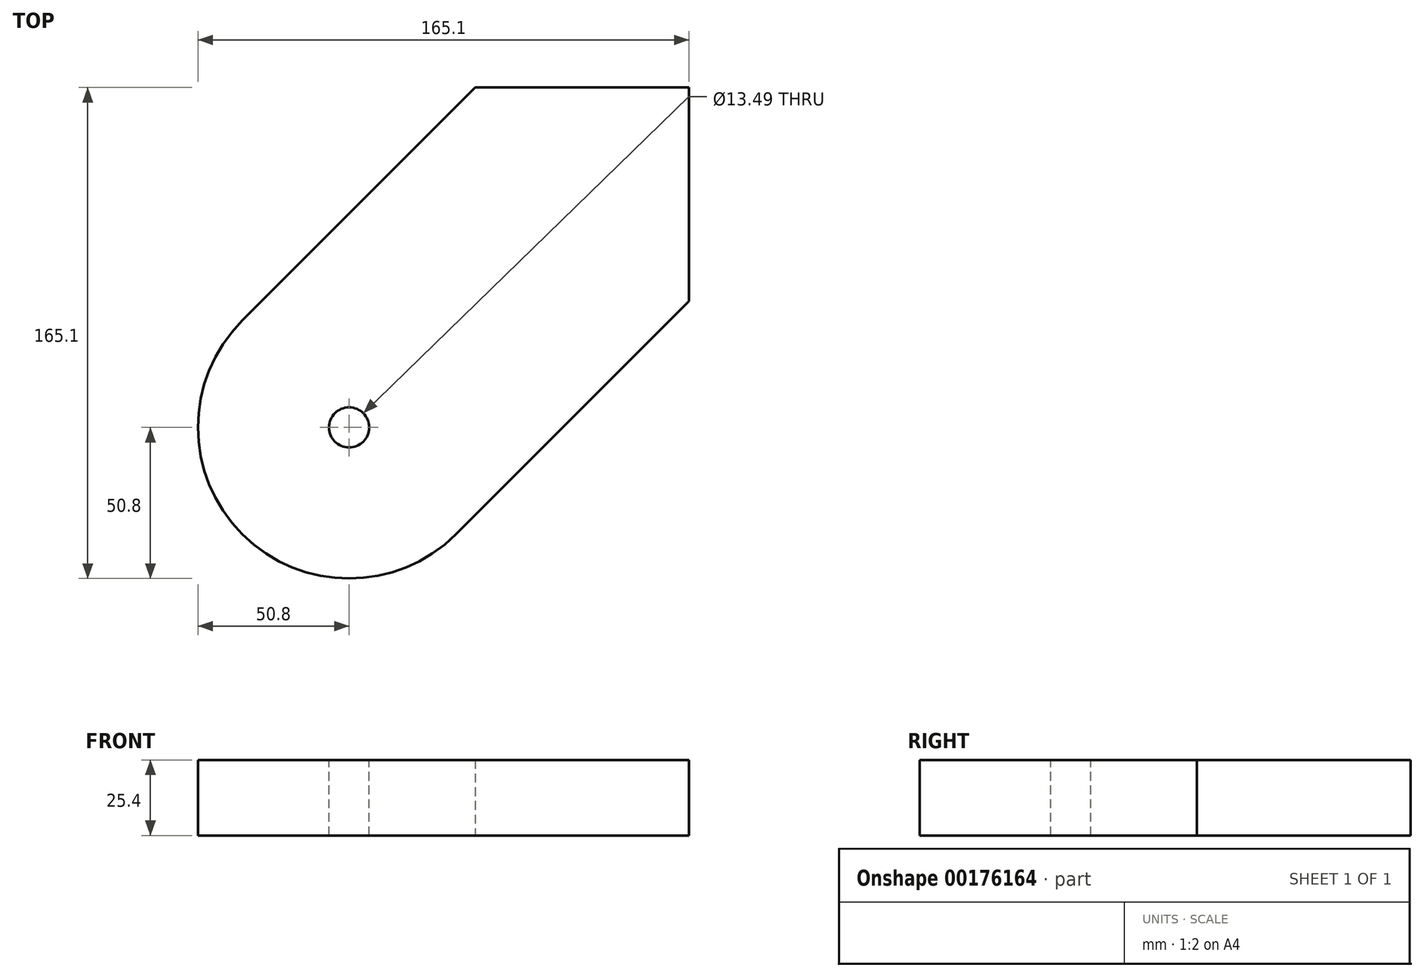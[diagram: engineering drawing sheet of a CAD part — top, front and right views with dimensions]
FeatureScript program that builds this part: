
annotation { "Feature Type Name" : "Feature", "Feature Type Description" : "" }
export const myFeature = defineFeature(function(context is Context, id is Id, definition is map)
    precondition{}
    {
        {
            var Q0;
            Q0=qCreatedBy(makeId("Top.planeOp"),FACE);
            var sketch = newSketch(context, id + "F0", { "sketchPlane" : qUnion([Q0])});
            skArc(sketch, "E0", {"start": v(-35.92, 35.92) * mm, "mid": v(-35.92, -35.92) * mm, "end": v(35.92, -35.92) * mm});
            skLineSegment(sketch, "E1", {"start": v(-35.92, 35.92) * mm, "end": v(42.46, 114.3) * mm});
            skLineSegment(sketch, "E2", {"start": v(42.46, 114.3) * mm, "end": v(114.3, 114.3) * mm});
            skLineSegment(sketch, "E3", {"start": v(114.3, 114.3) * mm, "end": v(114.3, 42.46) * mm});
            skLineSegment(sketch, "E4", {"start": v(114.3, 42.46) * mm, "end": v(35.92, -35.92) * mm});
            skSolve(sketch);
        }
        {
            var Q0;
            Q0 = qSketchRegion(id + "F0", true);
            extrude(context, id + "F1", {"entities" : qUnion([Q0]), "depth" : 25.4 * mm});
        }
        {
            var Q0;
            Q0=makeQuery(id+"F1.opExtrude","CAP_FACE",FACE,{"disambiguationData":[OSD([sQuery(id+"F0.wireOp",EDGE,"E0"),sQuery(id+"F0.wireOp",EDGE,"E1"),sQuery(id+"F0.wireOp",EDGE,"E2"),sQuery(id+"F0.wireOp",EDGE,"E3"),sQuery(id+"F0.wireOp",EDGE,"E4")])],"isStart":false});
            var sketch = newSketch(context, id + "F2", { "sketchPlane" : qUnion([Q0])});
            skPoint(sketch, "E5", {"position": v(0, 0) * mm});
            skSolve(sketch);
        }
        {
            var Q0;
            Q0=sQuery(id+"F2.wireOp",VERTEX,"E5");
            var Q1;
            Q1=makeQuery(id+"F1.opExtrude","SWEPT_BODY",BODY,{"disambiguationData":[OSD([sQuery(id+"F0.wireOp",EDGE,"E0"),sQuery(id+"F0.wireOp",EDGE,"E1"),sQuery(id+"F0.wireOp",EDGE,"E2"),sQuery(id+"F0.wireOp",EDGE,"E3"),sQuery(id+"F0.wireOp",EDGE,"E4")])]});
            hole(context, id + "F3", {"style" : HoleStyle.SIMPLE, "endStyle" : HoleEndStyle.THROUGH, "standardTappedOrClearance" : lookupTablePath({ "standard" : "ANSI", "fit" : "Normal (ASME)", "size" : "1/2", "type" : "Clearance" }), "standardBlindInLast" : lookupTablePath({ "fit" : "Free", "standard" : "ANSI", "size" : "1/2", "type" : "Clearance" }), "holeDiameter" : 13.5 * mm, "locations" : qUnion([Q0]), "scope" : qUnion([Q1]), "isTappedThrough" : true});
        }
    });
